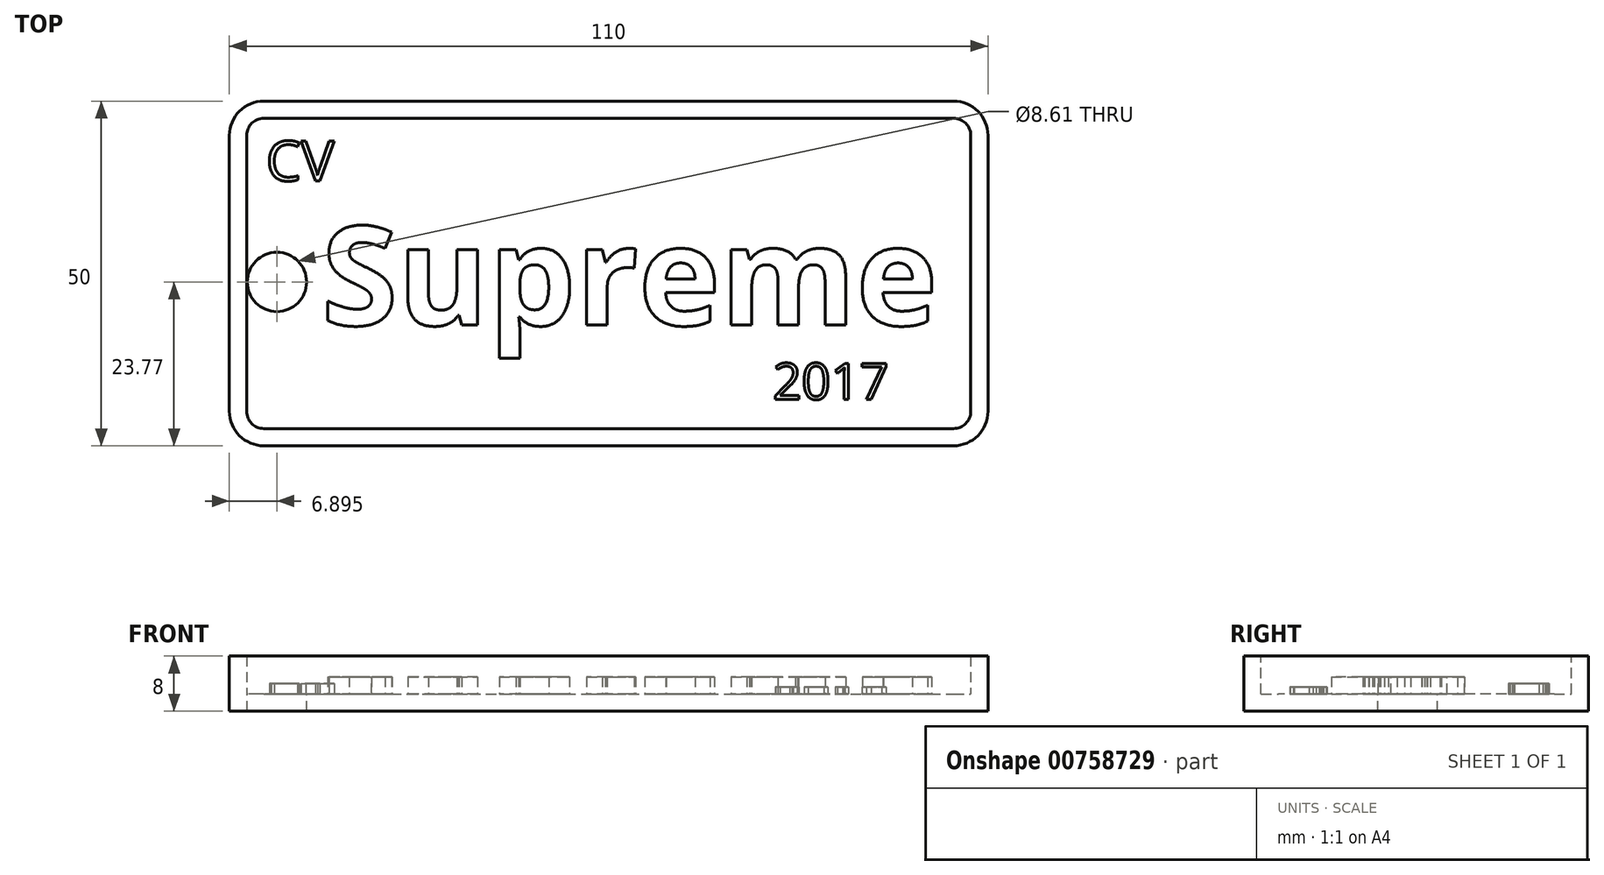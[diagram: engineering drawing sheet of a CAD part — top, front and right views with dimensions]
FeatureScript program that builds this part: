
annotation { "Feature Type Name" : "Feature", "Feature Type Description" : "" }
export const myFeature = defineFeature(function(context is Context, id is Id, definition is map)
    precondition{}
    {
        {
            var Q0;
            Q0=qCreatedBy(makeId("Top.planeOp"),FACE);
            var sketch = newSketch(context, id + "F0", { "sketchPlane" : qUnion([Q0])});
            skLineSegment(sketch, "E0.bottom", {"start": v(-64.9, 26.23) * mm, "end": v(45.1, 26.23) * mm});
            skLineSegment(sketch, "E0.top", {"start": v(-64.9, -23.77) * mm, "end": v(45.1, -23.77) * mm});
            skLineSegment(sketch, "E0.left", {"start": v(-64.9, 26.23) * mm, "end": v(-64.9, -23.77) * mm});
            skLineSegment(sketch, "E0.right", {"start": v(45.1, 26.23) * mm, "end": v(45.1, -23.77) * mm});
            skSolve(sketch);
        }
        {
            var Q0;
            Q0=makeQuery(id+"F0.imprint","IMPRINT",FACE,{"disambiguationData":[TD([[makeQuery(id+"F0.imprint","IMPRINT",EDGE,{"derivedFrom":sQuery(id+"F0.wireOp",EDGE,"E0.bottom")}),-1.0]])]});
            extrude(context, id + "F1", {"entities" : qUnion([Q0]), "depth" : 8 * mm, "offsetDistance" : 25 * mm});
        }
        {
            var Q0;
            Q0=makeQuery(id+"F1.opExtrude","SWEPT_EDGE",EDGE,{"disambiguationData":[OSD([sQuery(id+"F0.wireOp",EDGE,"E0.top"),sQuery(id+"F0.wireOp",EDGE,"E0.right")])]});
            var Q1;
            Q1=makeQuery(id+"F1.opExtrude","SWEPT_EDGE",EDGE,{"disambiguationData":[OSD([sQuery(id+"F0.wireOp",EDGE,"E0.bottom"),sQuery(id+"F0.wireOp",EDGE,"E0.right")])]});
            var Q2;
            Q2=makeQuery(id+"F1.opExtrude","SWEPT_EDGE",EDGE,{"disambiguationData":[OSD([sQuery(id+"F0.wireOp",EDGE,"E0.bottom"),sQuery(id+"F0.wireOp",EDGE,"E0.left")])]});
            var Q3;
            Q3=makeQuery(id+"F1.opExtrude","SWEPT_EDGE",EDGE,{"disambiguationData":[OSD([sQuery(id+"F0.wireOp",EDGE,"E0.top"),sQuery(id+"F0.wireOp",EDGE,"E0.left")])]});
            fillet(context, id + "F2", {"entities" : qUnion([Q0, Q1, Q2, Q3]), "radius" : 5 * mm, "tangentPropagation" : true, "allowEdgeOverflow" : false});
        }
        {
            var Q0;
            Q0=makeQuery(id+"F1.opExtrude","CAP_FACE",FACE,{"disambiguationData":[OSD([sQuery(id+"F0.wireOp",EDGE,"E0.bottom"),sQuery(id+"F0.wireOp",EDGE,"E0.top"),sQuery(id+"F0.wireOp",EDGE,"E0.left"),sQuery(id+"F0.wireOp",EDGE,"E0.right")])],"isStart":false});
            shell(context, id + "F3", {"entities" : qUnion([Q0]), "thickness" : 2.5 * mm});
        }
        {
            var Q0;
            Q0=makeQuery(id+"F3.opShell","OFFSET_FACE",FACE,{"disambiguationData":[OSD([sQuery(id+"F0.wireOp",EDGE,"E0.bottom"),sQuery(id+"F0.wireOp",EDGE,"E0.top"),sQuery(id+"F0.wireOp",EDGE,"E0.left"),sQuery(id+"F0.wireOp",EDGE,"E0.right")])]});
            var sketch = newSketch(context, id + "F4", { "sketchPlane" : qUnion([Q0])});
            skSolve(sketch);
        }
        {
            var Q0;
            {var subQ3=sQuery(id+"F0.wireOp",EDGE,"E0.bottom");Q0=makeQuery(id+"F4.imprint","IMPRINT",FACE,{"disambiguationData":[TD([[makeQuery(id+"F4.imprint","IMPRINT",EDGE,{"derivedFrom":makeQuery(id+"F3.opShell","OFFSET_EDGE",EDGE,{"disambiguationData":[OSD([subQ3]),TDD([makeQuery(id+"F1.opExtrude","CAP_EDGE",EDGE,{"disambiguationData":[OSD([subQ3])],"isStart":true})])]})}),-1.0]])]});}
            var sketch = newSketch(context, id + "F5", { "sketchPlane" : qUnion([Q0])});
            skCircle(sketch, "E1", {"center": v(-58, 0) * mm, "radius": 4.3 * mm});
            skSolve(sketch);
        }
        {
            var Q0;
            Q0 = qSketchRegion(id + "F5", true);
            extrude(context, id + "F6", {"entities" : qUnion([Q0]), "operationType" : NewBodyOperationType.REMOVE, "oppositeDirection" : true, "depth" : 25 * mm, "offsetDistance" : 25 * mm});
        }
        {
            var Q0;
            {var subQ3=sQuery(id+"F0.wireOp",EDGE,"E0.bottom");Q0=makeQuery(id+"F4.imprint","IMPRINT",FACE,{"disambiguationData":[TD([[makeQuery(id+"F4.imprint","IMPRINT",EDGE,{"derivedFrom":makeQuery(id+"F3.opShell","OFFSET_EDGE",EDGE,{"disambiguationData":[OSD([subQ3]),TDD([makeQuery(id+"F1.opExtrude","CAP_EDGE",EDGE,{"disambiguationData":[OSD([subQ3])],"isStart":true})])]})}),-1.0]])]});}
            var sketch = newSketch(context, id + "F7", { "sketchPlane" : qUnion([Q0])});
            skText(sketch, "E2", { "text": "Supreme", "fontName": "OpenSans-Bold.ttf"});
            const initialGuessF7  = {"E2": [-0.05155, -0.00627, 1, 0, 0.01443]};
            skSetInitialGuess(sketch, initialGuessF7);
            skSolve(sketch);
        }
        {
            var Q0;
            Q0 = qSketchRegion(id + "F7", true);
            extrude(context, id + "F8", {"entities" : qUnion([Q0]), "operationType" : NewBodyOperationType.ADD, "depth" : 2.5 * mm, "offsetDistance" : 25 * mm});
        }
        {
            var Q0;
            {var subQ3=sQuery(id+"F0.wireOp",EDGE,"E0.bottom");Q0=makeQuery(id+"F4.imprint","IMPRINT",FACE,{"disambiguationData":[TD([[makeQuery(id+"F4.imprint","IMPRINT",EDGE,{"derivedFrom":makeQuery(id+"F3.opShell","OFFSET_EDGE",EDGE,{"disambiguationData":[OSD([subQ3]),TDD([makeQuery(id+"F1.opExtrude","CAP_EDGE",EDGE,{"disambiguationData":[OSD([subQ3])],"isStart":true})])]})}),-1.0]])]});}
            var sketch = newSketch(context, id + "F9", { "sketchPlane" : qUnion([Q0])});
            skText(sketch, "E3", { "text": "CV", "fontName": "OpenSans-Regular.ttf"});
            const initialGuessF9  = {"E3": [-0.0596, 0.01467, 1, 0, 0.00581]};
            skSetInitialGuess(sketch, initialGuessF9);
            skSolve(sketch);
        }
        {
            var Q0;
            Q0 = qSketchRegion(id + "F9", true);
            extrude(context, id + "F10", {"entities" : qUnion([Q0]), "operationType" : NewBodyOperationType.ADD, "depth" : 1.5 * mm, "offsetDistance" : 25 * mm});
        }
        {
            var Q0;
            {var subQ3=sQuery(id+"F0.wireOp",EDGE,"E0.bottom");Q0=makeQuery(id+"F4.imprint","IMPRINT",FACE,{"disambiguationData":[TD([[makeQuery(id+"F4.imprint","IMPRINT",EDGE,{"derivedFrom":makeQuery(id+"F3.opShell","OFFSET_EDGE",EDGE,{"disambiguationData":[OSD([subQ3]),TDD([makeQuery(id+"F1.opExtrude","CAP_EDGE",EDGE,{"disambiguationData":[OSD([subQ3])],"isStart":true})])]})}),-1.0]])]});}
            var sketch = newSketch(context, id + "F11", { "sketchPlane" : qUnion([Q0])});
            skText(sketch, "E4", { "text": "2017", "fontName": "OpenSans-Regular.ttf"});
            const initialGuessF11  = {"E4": [0.01387, -0.01704, 1, 0, 0.00529]};
            skSetInitialGuess(sketch, initialGuessF11);
            skSolve(sketch);
        }
        {
            var Q0;
            Q0 = qSketchRegion(id + "F11", true);
            extrude(context, id + "F12", {"entities" : qUnion([Q0]), "operationType" : NewBodyOperationType.ADD, "depth" : 1 * mm, "offsetDistance" : 25 * mm});
        }
    });
